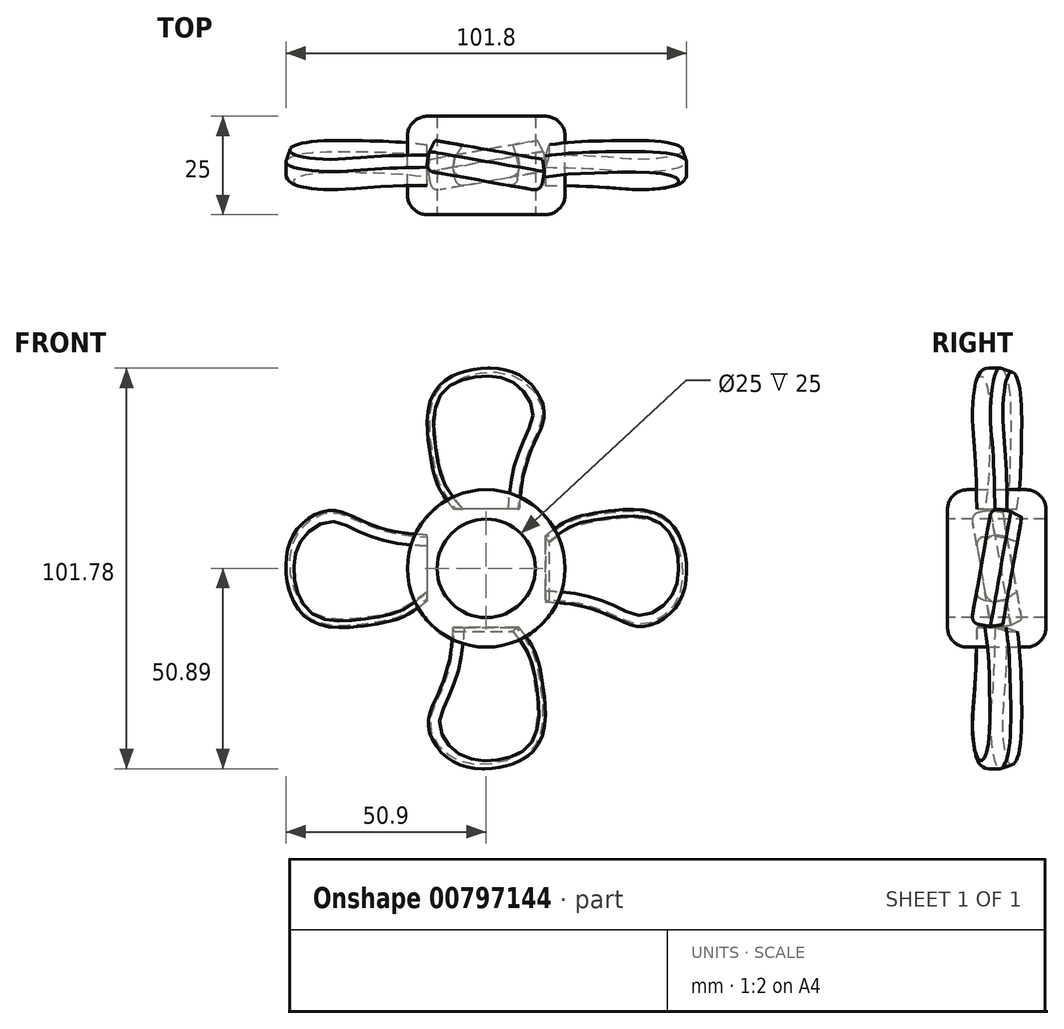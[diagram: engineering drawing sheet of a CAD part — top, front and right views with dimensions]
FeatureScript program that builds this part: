
annotation { "Feature Type Name" : "Feature", "Feature Type Description" : "" }
export const myFeature = defineFeature(function(context is Context, id is Id, definition is map)
    precondition{}
    {
        {
            var Q0;
            Q0=qCreatedBy(makeId("Front.planeOp"),FACE);
            var sketch = newSketch(context, id + "F0", { "sketchPlane" : qUnion([Q0])});
            skCircle(sketch, "E0", {"center": v(0, 0) * mm, "radius": 20 * mm});
            skSolve(sketch);
        }
        {
            var Q0;
            Q0=makeQuery(id+"F0.imprint","IMPRINT",FACE,{"disambiguationData":[TD([[makeQuery(id+"F0.imprint","IMPRINT",EDGE,{"derivedFrom":sQuery(id+"F0.wireOp",EDGE,"E0")}),1.0]])]});
            extrude(context, id + "F1", {"entities" : qUnion([Q0]), "endBound" : BoundingType.SYMMETRIC, "depth" : 25 * mm, "offsetDistance" : 25 * mm});
        }
        {
            var Q0;
            Q0=makeQuery(id+"F1.opExtrude","CAP_FACE",FACE,{"disambiguationData":[OSD([sQuery(id+"F0.wireOp",EDGE,"E0")])],"isStart":false});
            var sketch = newSketch(context, id + "F2", { "sketchPlane" : qUnion([Q0])});
            skCircle(sketch, "E1", {"center": v(0, 0) * mm, "radius": 12.5 * mm});
            skSolve(sketch);
        }
        {
            var Q0;
            Q0 = qSketchRegion(id + "F2", true);
            extrude(context, id + "F3", {"entities" : qUnion([Q0]), "operationType" : NewBodyOperationType.REMOVE, "endBound" : BoundingType.THROUGH_ALL, "oppositeDirection" : true, "depth" : 25 * mm, "offsetDistance" : 25 * mm});
        }
        {
            var Q0;
            Q0=qCreatedBy(makeId("Top.planeOp"),FACE);
            cPlane(context, id + "F4", {"entities" : qUnion([Q0]), "cplaneType" : CPlaneType.OFFSET, "offset" : 15 * mm, "width" : 150 * mm, "height" : 150 * mm});
        }
        {
            var Q0;
            Q0=qCreatedBy(makeId("Front.planeOp"),FACE);
            var sketch = newSketch(context, id + "F5", { "sketchPlane" : qUnion([Q0])});
            skLineSegment(sketch, "E2", {"start": v(0, 65.78) * mm, "end": v(0, -42.37) * mm});
            skSolve(sketch);
        }
        {
            var Q0;
            Q0=qCreatedBy(makeId("Front.planeOp"),FACE);
            var sketch = newSketch(context, id + "F6", { "sketchPlane" : qUnion([Q0])});
            skLineSegment(sketch, "E3", {"start": v(8.44, 30.04) * mm, "end": v(-8.04, 30.04) * mm});
            skFitSpline(sketch, "E4", {"points": [v(-8.04, 30.04) * mm, v(-12.14, 36.11) * mm, v(-14.2, 44.58) * mm, v(-14.71, 54.6) * mm, v(-10.86, 62.29) * mm, v(0, 65.88) * mm, v(9.92, 63.06) * mm, v(14.8, 54.85) * mm, v(12.5, 47.4) * mm, v(9.43, 38.73) * mm, v(8.44, 30.04) * mm], "startDerivative": vector(-51.68, 63.69) * mm, "endDerivative": vector(-5.5, -88.8) * mm});
            skSolve(sketch);
        }
        {
            var Q0;
            Q0=makeQuery(id+"F6.imprint","IMPRINT",FACE,{"disambiguationData":[TD([[makeQuery(id+"F6.imprint","IMPRINT",EDGE,{"derivedFrom":sQuery(id+"F6.wireOp",EDGE,"E3")}),-1.0]])]});
            extrude(context, id + "F7", {"entities" : qUnion([Q0]), "endBound" : BoundingType.SYMMETRIC, "depth" : 8 * mm, "offsetDistance" : 25 * mm});
        }
        {
            var Q0;
            Q0=makeQuery(id+"F7.opExtrude","SWEPT_BODY",BODY,{"disambiguationData":[OSD([sQuery(id+"F6.wireOp",EDGE,"E3"),sQuery(id+"F6.wireOp",EDGE,"E4")])]});
            var Q1;
            Q1=sQuery(id+"F5.wireOp",EDGE,"E2");
            var Q2;
            Q2=sQuery(id+"F5.wireOp",EDGE,"E2");
            transform(context, id + "F8", {"entities" : qUnion([Q0]), "transformType" : TransformType.ROTATION, "transformAxis" : qUnion([Q2]), "angle" : 10 * degree, "makeCopy" : false});
        }
        {
            var Q0;
            Q0=makeQuery(id+"F7.opExtrude","SWEPT_BODY",BODY,{"disambiguationData":[OSD([sQuery(id+"F6.wireOp",EDGE,"E3"),sQuery(id+"F6.wireOp",EDGE,"E4")])]});
            var Q1;
            Q1=qCreatedBy(id+"F4.planeOp",FACE);
            transform(context, id + "F9", {"entities" : qUnion([Q0]), "transformType" : TransformType.TRANSLATION_DISTANCE, "transformDirection" : qUnion([Q1]), "distance" : 15 * mm, "oppositeDirection" : true, "makeCopy" : false});
        }
        {
            var Q0;
            Q0=qCreatedBy(makeId("Top.planeOp"),FACE);
            var sketch = newSketch(context, id + "F10", { "sketchPlane" : qUnion([Q0])});
            skLineSegment(sketch, "E5", {"start": v(0, -41.28) * mm, "end": v(0, 38.92) * mm});
            skSolve(sketch);
        }
        {
            var Q0;
            Q0=makeQuery(id+"F7.opExtrude","SWEPT_BODY",BODY,{"disambiguationData":[OSD([sQuery(id+"F6.wireOp",EDGE,"E3"),sQuery(id+"F6.wireOp",EDGE,"E4")])]});
            var Q1;
            Q1=sQuery(id+"F10.wireOp",EDGE,"E5");
            circularPattern(context, id + "F11", {"entities" : qUnion([Q0]), "axis" : qUnion([Q1]), "angle" : 360 * degree, "instanceCount" : 4, "equalSpace" : true});
        }
        {
            var Q0;
            Q0=makeQuery(id+"F7.opExtrude","CAP_EDGE",EDGE,{"disambiguationData":[OSD([sQuery(id+"F6.wireOp",EDGE,"E4")])],"isStart":false});
            var Q1;
            Q1=makeQuery(id+"F11.opPattern","COPY",EDGE,{"derivedFrom":makeQuery(id+"F7.opExtrude","CAP_EDGE",EDGE,{"disambiguationData":[OSD([sQuery(id+"F6.wireOp",EDGE,"E4")])],"isStart":false}),"instanceName":"1"});
            var Q2;
            Q2=makeQuery(id+"F11.opPattern","COPY",EDGE,{"derivedFrom":makeQuery(id+"F7.opExtrude","CAP_EDGE",EDGE,{"disambiguationData":[OSD([sQuery(id+"F6.wireOp",EDGE,"E4")])],"isStart":false}),"instanceName":"3"});
            var Q3;
            Q3=makeQuery(id+"F11.opPattern","COPY",EDGE,{"derivedFrom":makeQuery(id+"F7.opExtrude","CAP_EDGE",EDGE,{"disambiguationData":[OSD([sQuery(id+"F6.wireOp",EDGE,"E4")])],"isStart":false}),"instanceName":"2"});
            fillet(context, id + "F12", {"entities" : qUnion([Q0, Q1, Q2, Q3]), "radius" : 2 * mm, "tangentPropagation" : true, "allowEdgeOverflow" : false});
        }
        {
            var Q0;
            Q0=makeQuery(id+"F7.opExtrude","CAP_EDGE",EDGE,{"disambiguationData":[OSD([sQuery(id+"F6.wireOp",EDGE,"E4")])],"isStart":true});
            var Q1;
            Q1=makeQuery(id+"F11.opPattern","COPY",EDGE,{"derivedFrom":makeQuery(id+"F7.opExtrude","CAP_EDGE",EDGE,{"disambiguationData":[OSD([sQuery(id+"F6.wireOp",EDGE,"E4")])],"isStart":true}),"instanceName":"3"});
            var Q2;
            Q2=makeQuery(id+"F11.opPattern","COPY",FACE,{"derivedFrom":makeQuery(id+"F7.opExtrude","CAP_FACE",FACE,{"disambiguationData":[OSD([sQuery(id+"F6.wireOp",EDGE,"E3"),sQuery(id+"F6.wireOp",EDGE,"E4")])],"isStart":true}),"instanceName":"2"});
            var Q3;
            Q3=makeQuery(id+"F11.opPattern","COPY",FACE,{"derivedFrom":makeQuery(id+"F7.opExtrude","CAP_FACE",FACE,{"disambiguationData":[OSD([sQuery(id+"F6.wireOp",EDGE,"E3"),sQuery(id+"F6.wireOp",EDGE,"E4")])],"isStart":true}),"instanceName":"1"});
            chamfer(context, id + "F13", {"entities" : qUnion([Q0, Q1, Q2, Q3]), "chamferType" : ChamferType.TWO_OFFSETS, "width1" : 1 * mm, "oppositeDirection" : false, "width2" : 3 * mm, "tangentPropagation" : true});
        }
        {
            var Q0;
            Q0=makeQuery(id+"F1.opExtrude","CAP_EDGE",EDGE,{"disambiguationData":[OSD([sQuery(id+"F0.wireOp",EDGE,"E0")])],"isStart":true});
            var Q1;
            Q1=makeQuery(id+"F1.opExtrude","CAP_EDGE",EDGE,{"disambiguationData":[OSD([sQuery(id+"F0.wireOp",EDGE,"E0")])],"isStart":false});
            fillet(context, id + "F14", {"entities" : qUnion([Q0, Q1]), "radius" : 5 * mm, "tangentPropagation" : true, "allowEdgeOverflow" : false});
        }
    });
